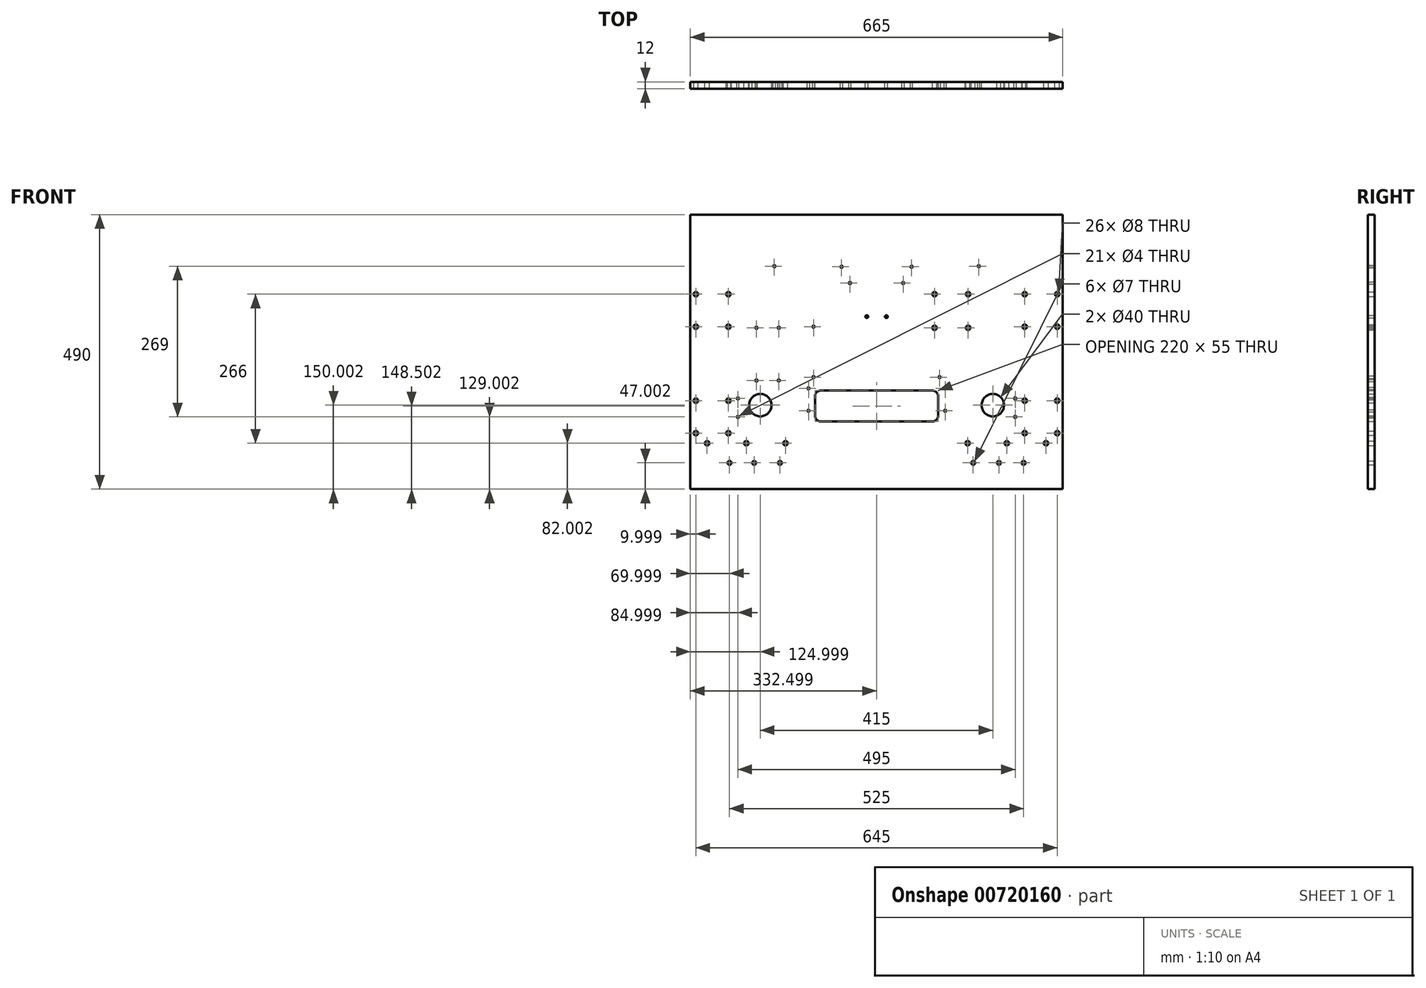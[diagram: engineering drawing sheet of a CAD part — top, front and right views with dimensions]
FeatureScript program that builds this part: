
annotation { "Feature Type Name" : "Feature", "Feature Type Description" : "" }
export const myFeature = defineFeature(function(context is Context, id is Id, definition is map)
    precondition{}
    {
        {
            var Q0;
            Q0=qCreatedBy(makeId("Front.planeOp"),FACE);
            var sketch = newSketch(context, id + "F0", { "sketchPlane" : qUnion([Q0])});
            skCircle(sketch, "E0", {"center": v(-221.14, -103.17) * mm, "radius": 2.07 * mm});
            skCircle(sketch, "E1", {"center": v(307.86, -161.17) * mm, "radius": 2 * mm});
            skCircle(sketch, "E2", {"center": v(-221.14, 28.83) * mm, "radius": 2 * mm});
            skCircle(sketch, "E3", {"center": v(307.86, 28.83) * mm, "radius": 2 * mm});
            skCircle(sketch, "E4", {"center": v(307.86, 86.83) * mm, "radius": 2 * mm});
            skCircle(sketch, "E5", {"center": v(307.86, -103.17) * mm, "radius": 2 * mm});
            skCircle(sketch, "E6", {"center": v(-221.14, -161.17) * mm, "radius": 2 * mm});
            skCircle(sketch, "E7", {"center": v(-221.14, 86.83) * mm, "radius": 2 * mm});
            skCircle(sketch, "E8", {"center": v(60.86, 46.83) * mm, "radius": 2.5 * mm});
            skCircle(sketch, "E9", {"center": v(25.86, 46.83) * mm, "radius": 2.5 * mm});
            skArc(sketch, "E10", {"start": v(-56.64, -85.17) * mm, "mid": v(-63.71, -88.1) * mm, "end": v(-66.64, -95.17) * mm});
            skLineSegment(sketch, "E11", {"start": v(-66.64, -130.17) * mm, "end": v(-66.64, -95.17) * mm});
            skArc(sketch, "E12", {"start": v(-66.64, -130.17) * mm, "mid": v(-63.71, -137.24) * mm, "end": v(-56.64, -140.17) * mm});
            skLineSegment(sketch, "E13", {"start": v(143.36, -140.17) * mm, "end": v(-56.64, -140.17) * mm});
            skArc(sketch, "E14", {"start": v(143.36, -140.17) * mm, "mid": v(150.43, -137.24) * mm, "end": v(153.36, -130.17) * mm});
            skLineSegment(sketch, "E15", {"start": v(153.36, -95.17) * mm, "end": v(153.36, -130.17) * mm});
            skArc(sketch, "E16", {"start": v(153.36, -95.17) * mm, "mid": v(150.43, -88.1) * mm, "end": v(143.36, -85.17) * mm});
            skLineSegment(sketch, "E17", {"start": v(-56.64, -85.17) * mm, "end": v(143.36, -85.17) * mm});
            skCircle(sketch, "E18", {"center": v(250.86, -111.17) * mm, "radius": 20 * mm});
            skCircle(sketch, "E19", {"center": v(-164.14, -111.17) * mm, "radius": 20 * mm});
            skCircle(sketch, "E20", {"center": v(165.86, -121.17) * mm, "radius": 2 * mm});
            skCircle(sketch, "E21", {"center": v(-78.14, -121.17) * mm, "radius": 2 * mm});
            skCircle(sketch, "E22", {"center": v(165.86, -81.17) * mm, "radius": 2 * mm});
            skCircle(sketch, "E23", {"center": v(-78.14, -81.16) * mm, "radius": 2 * mm});
            skCircle(sketch, "E24", {"center": v(90.86, 106.83) * mm, "radius": 2 * mm});
            skCircle(sketch, "E25", {"center": v(-4.14, 106.83) * mm, "radius": 2 * mm});
            skCircle(sketch, "E26", {"center": v(155.86, -61.17) * mm, "radius": 2 * mm});
            skCircle(sketch, "E27", {"center": v(275.86, -179.17) * mm, "radius": 2 * mm});
            skCircle(sketch, "E28", {"center": v(345.86, -179.17) * mm, "radius": 2 * mm});
            skCircle(sketch, "E29", {"center": v(290.86, -132.17) * mm, "radius": 2 * mm});
            skCircle(sketch, "E30", {"center": v(290.86, -99.17) * mm, "radius": 2 * mm});
            skCircle(sketch, "E31", {"center": v(-69.14, 28.83) * mm, "radius": 2 * mm});
            skCircle(sketch, "E32", {"center": v(-69.14, -61.17) * mm, "radius": 2 * mm});
            skCircle(sketch, "E33", {"center": v(-131.14, -67.05) * mm, "radius": 2 * mm});
            skCircle(sketch, "E34", {"center": v(-171.14, -67.05) * mm, "radius": 2 * mm});
            skCircle(sketch, "E35", {"center": v(-204.14, -132.17) * mm, "radius": 2 * mm});
            skCircle(sketch, "E36", {"center": v(-204.14, -99.17) * mm, "radius": 2 * mm});
            skCircle(sketch, "E37", {"center": v(-189.14, -179.17) * mm, "radius": 2 * mm});
            skCircle(sketch, "E38", {"center": v(-259.14, -179.17) * mm, "radius": 2 * mm});
            skCircle(sketch, "E39", {"center": v(205.86, -179.17) * mm, "radius": 2 * mm});
            skCircle(sketch, "E40", {"center": v(365.86, -161.17) * mm, "radius": 2 * mm});
            skCircle(sketch, "E41", {"center": v(365.86, -103.17) * mm, "radius": 2 * mm});
            skCircle(sketch, "E42", {"center": v(365.86, 28.83) * mm, "radius": 2 * mm});
            skCircle(sketch, "E43", {"center": v(365.86, 86.83) * mm, "radius": 2 * mm});
            skCircle(sketch, "E44", {"center": v(105.86, 135.83) * mm, "radius": 2 * mm});
            skCircle(sketch, "E45", {"center": v(225.86, 136.83) * mm, "radius": 2 * mm});
            skCircle(sketch, "E46", {"center": v(-19.14, 135.83) * mm, "radius": 2 * mm});
            skCircle(sketch, "E47", {"center": v(-139.14, 136.83) * mm, "radius": 2 * mm});
            skCircle(sketch, "E48", {"center": v(-119.14, -179.17) * mm, "radius": 2 * mm});
            skCircle(sketch, "E49", {"center": v(-279.14, -161.17) * mm, "radius": 2 * mm});
            skCircle(sketch, "E50", {"center": v(-279.14, -103.17) * mm, "radius": 2 * mm});
            skCircle(sketch, "E51", {"center": v(-279.14, 28.83) * mm, "radius": 2 * mm});
            skCircle(sketch, "E52", {"center": v(-279.14, 86.83) * mm, "radius": 2 * mm});
            skLineSegment(sketch, "E53", {"start": v(375.86, 228.83) * mm, "end": v(375.86, -261.17) * mm});
            skLineSegment(sketch, "E54", {"start": v(375.86, -261.17) * mm, "end": v(-289.14, -261.17) * mm});
            skLineSegment(sketch, "E55", {"start": v(-289.14, -261.17) * mm, "end": v(-289.14, 228.83) * mm});
            skLineSegment(sketch, "E56", {"start": v(-289.14, 228.83) * mm, "end": v(375.86, 228.83) * mm});
            skCircle(sketch, "E57", {"center": v(-131.14, 26.95) * mm, "radius": 2 * mm});
            skCircle(sketch, "E58", {"center": v(-171.14, 26.95) * mm, "radius": 2 * mm});
            skCircle(sketch, "E59", {"center": v(146.86, 26.83) * mm, "radius": 2 * mm});
            skCircle(sketch, "E60", {"center": v(206.86, 26.83) * mm, "radius": 2 * mm});
            skCircle(sketch, "E61", {"center": v(146.86, 86.83) * mm, "radius": 2 * mm});
            skCircle(sketch, "E62", {"center": v(206.86, 86.83) * mm, "radius": 2 * mm});
            skCircle(sketch, "E63", {"center": v(-219.14, -214.17) * mm, "radius": 3.5 * mm});
            skCircle(sketch, "E64", {"center": v(-175.14, -214.17) * mm, "radius": 3.5 * mm});
            skCircle(sketch, "E65", {"center": v(-129.14, -214.17) * mm, "radius": 3.5 * mm});
            skCircle(sketch, "E66", {"center": v(305.86, -214.17) * mm, "radius": 3.5 * mm});
            skCircle(sketch, "E67", {"center": v(261.86, -214.17) * mm, "radius": 3.5 * mm});
            skCircle(sketch, "E68", {"center": v(215.86, -214.17) * mm, "radius": 3.5 * mm});
            skCircle(sketch, "E69", {"center": v(307.86, 86.83) * mm, "radius": 4 * mm});
            skCircle(sketch, "E70.0.1.0", {"center": v(307.86, 28.83) * mm, "radius": 4 * mm});
            skCircle(sketch, "E70.1.0.0", {"center": v(365.86, 86.83) * mm, "radius": 4 * mm});
            skCircle(sketch, "E70.1.1.0", {"center": v(365.86, 28.83) * mm, "radius": 4 * mm});
            skLineSegment(sketch, "E70.direction1", {"start": v(307.86, 86.83) * mm, "end": v(365.86, 86.83) * mm, "construction": true});
            skLineSegment(sketch, "E70.direction2", {"start": v(307.86, 86.83) * mm, "end": v(307.86, 28.83) * mm, "construction": true});
            skCircle(sketch, "E71", {"center": v(307.86, -103.17) * mm, "radius": 4 * mm});
            skCircle(sketch, "E72.0.1.0", {"center": v(307.86, -161.17) * mm, "radius": 4 * mm});
            skCircle(sketch, "E72.1.0.0", {"center": v(365.86, -103.17) * mm, "radius": 4 * mm});
            skCircle(sketch, "E72.1.1.0", {"center": v(365.86, -161.17) * mm, "radius": 4 * mm});
            skLineSegment(sketch, "E72.direction1", {"start": v(307.86, -103.17) * mm, "end": v(365.86, -103.17) * mm, "construction": true});
            skLineSegment(sketch, "E72.direction2", {"start": v(307.86, -103.17) * mm, "end": v(307.86, -161.17) * mm, "construction": true});
            skCircle(sketch, "E73", {"center": v(-279.14, -103.17) * mm, "radius": 4 * mm});
            skCircle(sketch, "E74.0.1.0", {"center": v(-279.14, -161.17) * mm, "radius": 4 * mm});
            skCircle(sketch, "E74.1.0.0", {"center": v(-221.14, -103.17) * mm, "radius": 4 * mm});
            skCircle(sketch, "E74.1.1.0", {"center": v(-221.14, -161.17) * mm, "radius": 4 * mm});
            skLineSegment(sketch, "E74.direction1", {"start": v(-279.14, -103.17) * mm, "end": v(-221.14, -103.17) * mm, "construction": true});
            skLineSegment(sketch, "E74.direction2", {"start": v(-279.14, -103.17) * mm, "end": v(-279.14, -161.17) * mm, "construction": true});
            skCircle(sketch, "E75", {"center": v(-279.14, 86.83) * mm, "radius": 4 * mm});
            skCircle(sketch, "E76.0.1.0", {"center": v(-279.14, 28.83) * mm, "radius": 4 * mm});
            skCircle(sketch, "E76.1.0.0", {"center": v(-221.14, 86.83) * mm, "radius": 4 * mm});
            skCircle(sketch, "E76.1.1.0", {"center": v(-221.14, 28.83) * mm, "radius": 4 * mm});
            skLineSegment(sketch, "E76.direction1", {"start": v(-279.14, 86.83) * mm, "end": v(-221.14, 86.83) * mm, "construction": true});
            skLineSegment(sketch, "E76.direction2", {"start": v(-279.14, 86.83) * mm, "end": v(-279.14, 28.83) * mm, "construction": true});
            skCircle(sketch, "E77", {"center": v(146.86, 86.83) * mm, "radius": 4 * mm});
            skCircle(sketch, "E78.0.1.0", {"center": v(146.86, 26.83) * mm, "radius": 4 * mm});
            skCircle(sketch, "E78.1.0.0", {"center": v(206.86, 86.83) * mm, "radius": 4 * mm});
            skCircle(sketch, "E78.1.1.0", {"center": v(206.86, 26.83) * mm, "radius": 4 * mm});
            skLineSegment(sketch, "E78.direction1", {"start": v(146.86, 86.83) * mm, "end": v(206.86, 86.83) * mm, "construction": true});
            skLineSegment(sketch, "E78.direction2", {"start": v(146.86, 86.83) * mm, "end": v(146.86, 26.83) * mm, "construction": true});
            skCircle(sketch, "E79", {"center": v(-259.14, -179.17) * mm, "radius": 4 * mm});
            skCircle(sketch, "E80", {"center": v(-189.14, -179.17) * mm, "radius": 4 * mm});
            skCircle(sketch, "E81", {"center": v(-119.14, -179.17) * mm, "radius": 4 * mm});
            skCircle(sketch, "E82", {"center": v(205.86, -179.17) * mm, "radius": 4 * mm});
            skCircle(sketch, "E83", {"center": v(275.86, -179.17) * mm, "radius": 4 * mm});
            skCircle(sketch, "E84", {"center": v(345.86, -179.17) * mm, "radius": 4 * mm});
            skSolve(sketch);
        }
        {
            var Q0;
            Q0 = qSketchRegion(id + "F0", true);
            extrude(context, id + "F1", {"entities" : qUnion([Q0]), "depth" : 12 * mm, "offsetDistance" : 25 * mm});
        }
    });
